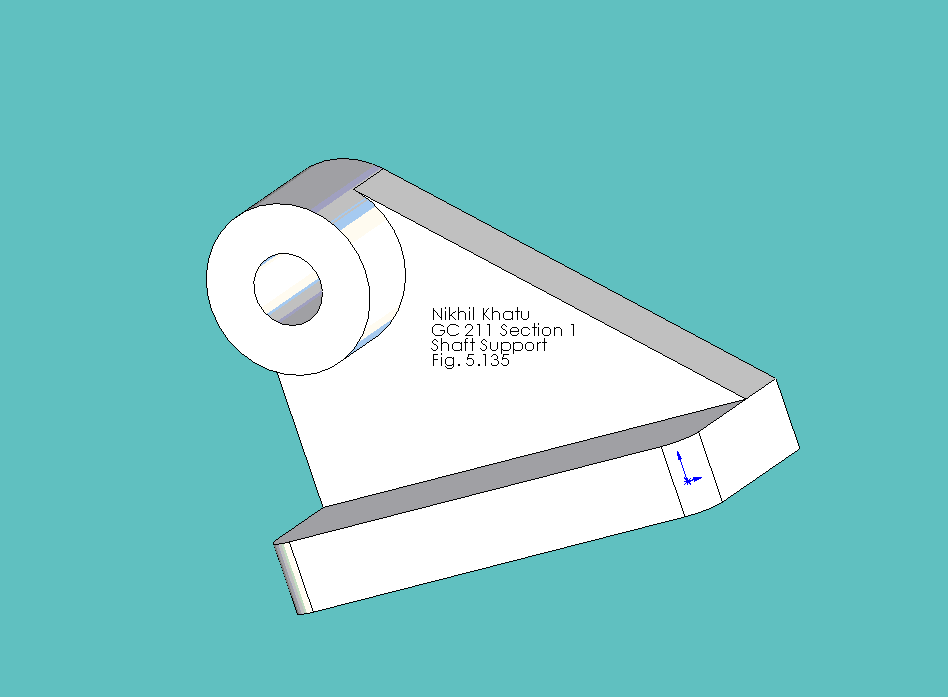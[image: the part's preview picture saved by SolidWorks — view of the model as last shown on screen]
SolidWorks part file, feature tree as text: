
SOLIDWORKS PART (.sldprt)
format: sldprt  version: not decoded by parser v0  size: 317,952 bytes
history: native  units: mm
features: sketch x6, plane x3, extrude x3, cut_extrude x3, material x1, fillet x1 (+11 scaffold rows collapsed)
feature tree (28):
  scaffold x11  (default folders/planes/origin — collapsed)
  material  "Zoltek Panex 33"
  plane  "Frontal"
  plane  "Horizontal"
  plane  "Profile"
  sketch  "Sketch1"  dims[D1=104.902mm D2=47.752mm]
  extrude  "Extrude1"  Depth=16.002mm
  fillet  "Fillet1"  Radius=6.35mm
  sketch  "Sketch2"  dims[D1=16.002mm D2=0.0mm]
  extrude  "Extrude2"  Depth=69.85mm
  sketch  "Sketch3"  dims[D2=38.1mm D1=85.852mm D3=50.8mm]
  cut_extrude  "Cut-Extrude1"  Depth=69.85mm
  sketch  "Sketch4"
  cut_extrude  "Cut-Extrude3"  [1 undecoded]
  sketch  "Sketch5"
  extrude  "Extrude3"  Depth=19.05mm
  sketch  "Sketch6"  dims[D1=~9.457617mm]
  cut_extrude  "Cut-Extrude4"  [1 undecoded]
decode coverage: 9 of 13 modeling features carry decoded parameters
note: ~ marks probable driven/reference dimensions
note: 2 parameter values undecoded
note: suppression state not decoded; provenance and decode notes live in map.json
